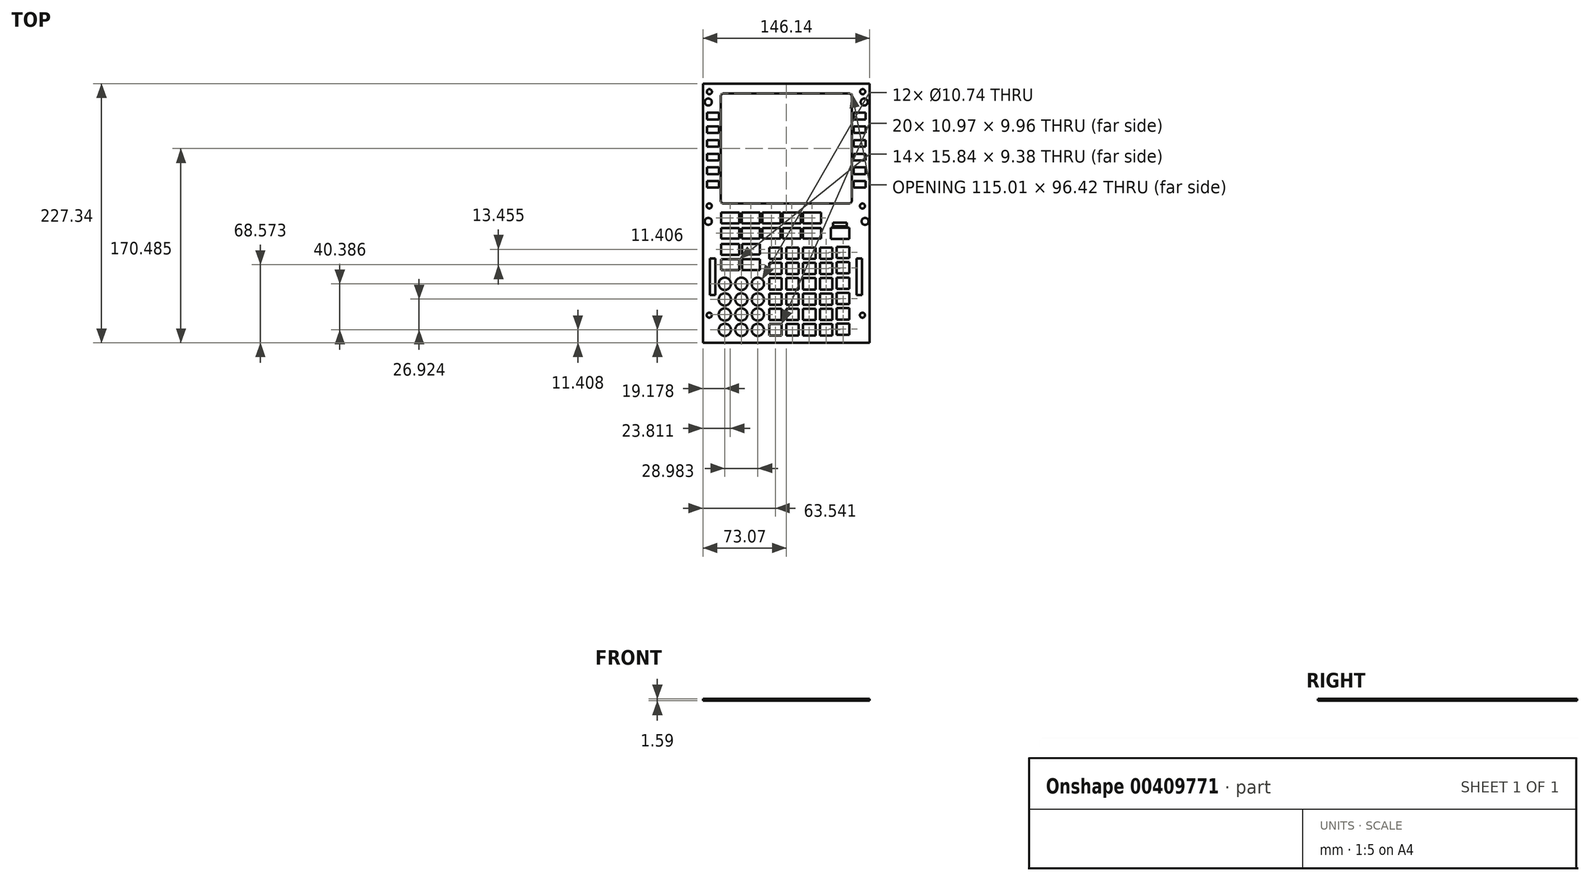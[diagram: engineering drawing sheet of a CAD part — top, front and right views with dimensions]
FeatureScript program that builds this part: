
annotation { "Feature Type Name" : "Feature", "Feature Type Description" : "" }
export const myFeature = defineFeature(function(context is Context, id is Id, definition is map)
    precondition{}
    {
        {
            var Q0;
            Q0=qCreatedBy(makeId("Top.planeOp"),FACE);
            var sketch = newSketch(context, id + "F0", { "sketchPlane" : qUnion([Q0])});
            skLineSegment(sketch, "E0.bottom", {"start": v(73.07, 113.67) * mm, "end": v(-73.07, 113.67) * mm});
            skLineSegment(sketch, "E0.top", {"start": v(73.07, -113.66) * mm, "end": v(-73.07, -113.66) * mm});
            skLineSegment(sketch, "E0.left", {"start": v(73.07, 113.67) * mm, "end": v(73.07, -113.66) * mm});
            skLineSegment(sketch, "E0.right", {"start": v(-73.07, 113.67) * mm, "end": v(-73.07, -113.66) * mm});
            skPoint(sketch, "E0.middle", {"position": v(0, 0) * mm});
            skLineSegment(sketch, "E1", {"start": v(0, 113.67) * mm, "end": v(0, 111.74) * mm});
            skLineSegment(sketch, "E2", {"start": v(-69.57, 102.01) * mm, "end": v(-68.34, 102.01) * mm});
            skLineSegment(sketch, "E3", {"start": v(-68.34, 93.24) * mm, "end": v(-69.57, 93.24) * mm});
            skLineSegment(sketch, "E4", {"start": v(-72.11, 90.7) * mm, "end": v(-72.11, 2.93) * mm});
            skLineSegment(sketch, "E5", {"start": v(-69.57, 0.4) * mm, "end": v(-66.53, 0.4) * mm});
            skLineSegment(sketch, "E6", {"start": v(-63.99, -2.15) * mm, "end": v(-63.99, -30.43) * mm});
            skLineSegment(sketch, "E7", {"start": v(-66.53, -32.97) * mm, "end": v(-68.15, -32.97) * mm});
            skLineSegment(sketch, "E8", {"start": v(-70.69, -35.51) * mm, "end": v(-70.69, -91.63) * mm});
            skLineSegment(sketch, "E9", {"start": v(-68.15, -94.17) * mm, "end": v(-64.1, -94.17) * mm});
            skLineSegment(sketch, "E10", {"start": v(-61.57, -96.71) * mm, "end": v(-61.57, -107.92) * mm});
            skLineSegment(sketch, "E11", {"start": v(-59.03, -110.46) * mm, "end": v(0, -110.46) * mm});
            skLineSegment(sketch, "E12", {"start": v(-72.11, 110.47) * mm, "end": v(-72.11, 108.94) * mm});
            skLineSegment(sketch, "E13", {"start": v(-70.84, 111.74) * mm, "end": v(-69.31, 111.74) * mm});
            skLineSegment(sketch, "E14", {"start": v(-72.11, 108.94) * mm, "end": v(-72.11, 104.55) * mm});
            skLineSegment(sketch, "E15", {"start": v(-69.31, 111.74) * mm, "end": v(0, 111.74) * mm});
            skPoint(sketch, "E16.visualSharp", {"position": v(-72.11, 111.74) * mm});
            skArc(sketch, "E16.filletArc", {"start": v(-70.84, 111.74) * mm, "mid": v(-71.74, 111.36) * mm, "end": v(-72.11, 110.47) * mm});
            skArc(sketch, "E17", {"start": v(-68.34, 93.24) * mm, "mid": v(-63.95, 97.62) * mm, "end": v(-68.34, 102.01) * mm});
            skPoint(sketch, "E18.visualSharp", {"position": v(-61.57, -110.46) * mm});
            skArc(sketch, "E18.filletArc", {"start": v(-61.57, -107.92) * mm, "mid": v(-60.82, -109.71) * mm, "end": v(-59.03, -110.46) * mm});
            skPoint(sketch, "E19.visualSharp", {"position": v(-61.57, -94.17) * mm});
            skArc(sketch, "E19.filletArc", {"start": v(-61.57, -96.71) * mm, "mid": v(-62.31, -94.92) * mm, "end": v(-64.1, -94.17) * mm});
            skPoint(sketch, "E20.visualSharp", {"position": v(-70.69, -94.17) * mm});
            skArc(sketch, "E20.filletArc", {"start": v(-70.69, -91.63) * mm, "mid": v(-69.94, -93.43) * mm, "end": v(-68.15, -94.17) * mm});
            skPoint(sketch, "E21.visualSharp", {"position": v(-70.69, -32.97) * mm});
            skArc(sketch, "E21.filletArc", {"start": v(-68.15, -32.97) * mm, "mid": v(-69.94, -33.72) * mm, "end": v(-70.69, -35.51) * mm});
            skPoint(sketch, "E22.visualSharp", {"position": v(-63.99, -32.97) * mm});
            skArc(sketch, "E22.filletArc", {"start": v(-66.53, -32.97) * mm, "mid": v(-64.73, -32.23) * mm, "end": v(-63.99, -30.43) * mm});
            skPoint(sketch, "E23.visualSharp", {"position": v(-63.99, 0.4) * mm});
            skArc(sketch, "E23.filletArc", {"start": v(-63.99, -2.15) * mm, "mid": v(-64.73, -0.35) * mm, "end": v(-66.53, 0.4) * mm});
            skPoint(sketch, "E24.visualSharp", {"position": v(-72.11, 0.4) * mm});
            skArc(sketch, "E24.filletArc", {"start": v(-72.11, 2.93) * mm, "mid": v(-71.37, 1.14) * mm, "end": v(-69.57, 0.4) * mm});
            skPoint(sketch, "E25.visualSharp", {"position": v(-72.11, 102.01) * mm});
            skArc(sketch, "E25.filletArc", {"start": v(-72.11, 104.55) * mm, "mid": v(-71.37, 102.76) * mm, "end": v(-69.57, 102.01) * mm});
            skPoint(sketch, "E26.visualSharp", {"position": v(-72.11, 93.24) * mm});
            skArc(sketch, "E26.filletArc", {"start": v(-69.57, 93.24) * mm, "mid": v(-71.37, 92.5) * mm, "end": v(-72.11, 90.7) * mm});
            skLineSegment(sketch, "E27.bottom", {"start": v(-59, 22.55) * mm, "end": v(-69.41, 22.55) * mm});
            skLineSegment(sketch, "E27.top", {"start": v(-59, 28.39) * mm, "end": v(-69.41, 28.39) * mm});
            skLineSegment(sketch, "E27.left", {"start": v(-59, 22.55) * mm, "end": v(-59, 28.39) * mm});
            skLineSegment(sketch, "E27.right", {"start": v(-69.41, 22.55) * mm, "end": v(-69.41, 28.39) * mm});
            skPoint(sketch, "E27.middle", {"position": v(-64.2, 25.47) * mm});
            skLineSegment(sketch, "E28.bottom", {"start": v(-59, 34.4) * mm, "end": v(-69.41, 34.4) * mm});
            skLineSegment(sketch, "E28.top", {"start": v(-59, 40.25) * mm, "end": v(-69.41, 40.25) * mm});
            skLineSegment(sketch, "E28.left", {"start": v(-59, 34.4) * mm, "end": v(-59, 40.25) * mm});
            skLineSegment(sketch, "E28.right", {"start": v(-69.41, 34.4) * mm, "end": v(-69.41, 40.25) * mm});
            skPoint(sketch, "E28.middle", {"position": v(-64.2, 37.33) * mm});
            skLineSegment(sketch, "E29.bottom", {"start": v(-59, 46.4) * mm, "end": v(-69.41, 46.4) * mm});
            skLineSegment(sketch, "E29.top", {"start": v(-59, 52.23) * mm, "end": v(-69.41, 52.23) * mm});
            skLineSegment(sketch, "E29.left", {"start": v(-59, 46.4) * mm, "end": v(-59, 52.23) * mm});
            skLineSegment(sketch, "E29.right", {"start": v(-69.41, 46.4) * mm, "end": v(-69.41, 52.23) * mm});
            skPoint(sketch, "E29.middle", {"position": v(-64.2, 49.31) * mm});
            skLineSegment(sketch, "E30.bottom", {"start": v(-59, 58.39) * mm, "end": v(-69.42, 58.39) * mm});
            skLineSegment(sketch, "E30.top", {"start": v(-59, 64.26) * mm, "end": v(-69.42, 64.26) * mm});
            skLineSegment(sketch, "E30.left", {"start": v(-59, 58.39) * mm, "end": v(-59, 64.26) * mm});
            skLineSegment(sketch, "E30.right", {"start": v(-69.42, 58.39) * mm, "end": v(-69.42, 64.26) * mm});
            skPoint(sketch, "E30.middle", {"position": v(-64.2, 61.32) * mm});
            skLineSegment(sketch, "E31.bottom", {"start": v(-59, 70.4) * mm, "end": v(-69.42, 70.4) * mm});
            skLineSegment(sketch, "E31.top", {"start": v(-59, 76.26) * mm, "end": v(-69.42, 76.26) * mm});
            skLineSegment(sketch, "E31.left", {"start": v(-59, 70.4) * mm, "end": v(-59, 76.26) * mm});
            skLineSegment(sketch, "E31.right", {"start": v(-69.42, 70.4) * mm, "end": v(-69.42, 76.26) * mm});
            skPoint(sketch, "E31.middle", {"position": v(-64.2, 73.33) * mm});
            skLineSegment(sketch, "E32.bottom", {"start": v(-59, 82.37) * mm, "end": v(-69.42, 82.37) * mm});
            skLineSegment(sketch, "E32.top", {"start": v(-59, 88.2) * mm, "end": v(-69.42, 88.2) * mm});
            skLineSegment(sketch, "E32.left", {"start": v(-59, 82.37) * mm, "end": v(-59, 88.2) * mm});
            skLineSegment(sketch, "E32.right", {"start": v(-69.42, 82.37) * mm, "end": v(-69.42, 88.2) * mm});
            skPoint(sketch, "E32.middle", {"position": v(-64.2, 85.29) * mm});
            skLineSegment(sketch, "E33", {"start": v(0, 100.27) * mm, "end": v(-50.04, 100.27) * mm});
            skLineSegment(sketch, "E34", {"start": v(-52.58, 97.73) * mm, "end": v(-52.58, 17.05) * mm});
            skLineSegment(sketch, "E35", {"start": v(-50.04, 14.51) * mm, "end": v(0, 14.51) * mm});
            skPoint(sketch, "E36.visualSharp", {"position": v(-52.58, 14.51) * mm});
            skArc(sketch, "E36.filletArc", {"start": v(-52.58, 17.05) * mm, "mid": v(-51.83, 15.26) * mm, "end": v(-50.04, 14.51) * mm});
            skPoint(sketch, "E37.visualSharp", {"position": v(-52.58, 100.27) * mm});
            skArc(sketch, "E37.filletArc", {"start": v(-50.04, 100.27) * mm, "mid": v(-51.83, 99.53) * mm, "end": v(-52.58, 97.73) * mm});
            skLineSegment(sketch, "E38", {"start": v(0, 105.03) * mm, "end": v(-54.96, 105.03) * mm});
            skLineSegment(sketch, "E39", {"start": v(-57.5, 102.49) * mm, "end": v(-57.5, 11.14) * mm});
            skLineSegment(sketch, "E40", {"start": v(-54.96, 8.6) * mm, "end": v(0, 8.6) * mm});
            skLineSegment(sketch, "E41.MirrorCS", {"start": v(59.03, -110.46) * mm, "end": v(0, -110.46) * mm});
            skArc(sketch, "E42.MirrorCS", {"start": v(61.57, -107.92) * mm, "mid": v(60.82, -109.71) * mm, "end": v(59.03, -110.46) * mm});
            skLineSegment(sketch, "E43.MirrorCS", {"start": v(61.57, -96.71) * mm, "end": v(61.57, -107.92) * mm});
            skArc(sketch, "E44.MirrorCS", {"start": v(61.57, -96.71) * mm, "mid": v(62.31, -94.92) * mm, "end": v(64.1, -94.17) * mm});
            skLineSegment(sketch, "E45.MirrorCS", {"start": v(68.15, -94.17) * mm, "end": v(64.1, -94.17) * mm});
            skArc(sketch, "E46.MirrorCS", {"start": v(70.69, -91.63) * mm, "mid": v(69.94, -93.43) * mm, "end": v(68.15, -94.17) * mm});
            skLineSegment(sketch, "E47.MirrorCS", {"start": v(70.69, -35.51) * mm, "end": v(70.69, -91.63) * mm});
            skArc(sketch, "E48.MirrorCS", {"start": v(68.15, -32.97) * mm, "mid": v(69.94, -33.72) * mm, "end": v(70.69, -35.51) * mm});
            skLineSegment(sketch, "E49.MirrorCS", {"start": v(66.53, -32.97) * mm, "end": v(68.15, -32.97) * mm});
            skArc(sketch, "E50.MirrorCS", {"start": v(66.53, -32.97) * mm, "mid": v(64.73, -32.23) * mm, "end": v(63.99, -30.43) * mm});
            skLineSegment(sketch, "E51.MirrorCS", {"start": v(63.99, -2.15) * mm, "end": v(63.99, -30.43) * mm});
            skArc(sketch, "E52.MirrorCS", {"start": v(63.99, -2.15) * mm, "mid": v(64.73, -0.35) * mm, "end": v(66.53, 0.4) * mm});
            skLineSegment(sketch, "E53.MirrorCS", {"start": v(69.57, 0.4) * mm, "end": v(66.53, 0.4) * mm});
            skArc(sketch, "E54.MirrorCS", {"start": v(72.11, 2.93) * mm, "mid": v(71.37, 1.14) * mm, "end": v(69.57, 0.4) * mm});
            skLineSegment(sketch, "E55.MirrorCS", {"start": v(72.11, 90.7) * mm, "end": v(72.11, 2.93) * mm});
            skLineSegment(sketch, "E56.MirrorCS", {"start": v(69.41, 22.55) * mm, "end": v(69.41, 28.39) * mm});
            skLineSegment(sketch, "E57.MirrorCS", {"start": v(59, 22.55) * mm, "end": v(69.41, 22.55) * mm});
            skLineSegment(sketch, "E58.MirrorCS", {"start": v(59, 22.55) * mm, "end": v(59, 28.39) * mm});
            skLineSegment(sketch, "E59.MirrorCS", {"start": v(59, 28.39) * mm, "end": v(69.41, 28.39) * mm});
            skLineSegment(sketch, "E60.MirrorCS", {"start": v(59, 34.4) * mm, "end": v(69.41, 34.4) * mm});
            skLineSegment(sketch, "E61.MirrorCS", {"start": v(59, 34.4) * mm, "end": v(59, 40.25) * mm});
            skLineSegment(sketch, "E62.MirrorCS", {"start": v(59, 40.25) * mm, "end": v(69.41, 40.25) * mm});
            skLineSegment(sketch, "E63.MirrorCS", {"start": v(69.41, 34.4) * mm, "end": v(69.41, 40.25) * mm});
            skLineSegment(sketch, "E64.MirrorCS", {"start": v(59, 46.4) * mm, "end": v(69.41, 46.4) * mm});
            skLineSegment(sketch, "E65.MirrorCS", {"start": v(59, 46.4) * mm, "end": v(59, 52.23) * mm});
            skLineSegment(sketch, "E66.MirrorCS", {"start": v(59, 52.23) * mm, "end": v(69.41, 52.23) * mm});
            skLineSegment(sketch, "E67.MirrorCS", {"start": v(69.41, 46.4) * mm, "end": v(69.41, 52.23) * mm});
            skLineSegment(sketch, "E68.MirrorCS", {"start": v(59, 58.39) * mm, "end": v(69.42, 58.39) * mm});
            skLineSegment(sketch, "E69.MirrorCS", {"start": v(69.42, 58.39) * mm, "end": v(69.42, 64.26) * mm});
            skLineSegment(sketch, "E70.MirrorCS", {"start": v(59, 64.26) * mm, "end": v(69.42, 64.26) * mm});
            skLineSegment(sketch, "E71.MirrorCS", {"start": v(59, 58.39) * mm, "end": v(59, 64.26) * mm});
            skLineSegment(sketch, "E72.MirrorCS", {"start": v(59, 70.4) * mm, "end": v(69.42, 70.4) * mm});
            skLineSegment(sketch, "E73.MirrorCS", {"start": v(69.42, 70.4) * mm, "end": v(69.42, 76.26) * mm});
            skLineSegment(sketch, "E74.MirrorCS", {"start": v(59, 76.26) * mm, "end": v(69.42, 76.26) * mm});
            skLineSegment(sketch, "E75.MirrorCS", {"start": v(59, 70.4) * mm, "end": v(59, 76.26) * mm});
            skLineSegment(sketch, "E76.MirrorCS", {"start": v(59, 82.37) * mm, "end": v(69.42, 82.37) * mm});
            skLineSegment(sketch, "E77.MirrorCS", {"start": v(69.42, 82.37) * mm, "end": v(69.42, 88.2) * mm});
            skLineSegment(sketch, "E78.MirrorCS", {"start": v(59, 88.2) * mm, "end": v(69.42, 88.2) * mm});
            skLineSegment(sketch, "E79.MirrorCS", {"start": v(59, 82.37) * mm, "end": v(59, 88.2) * mm});
            skArc(sketch, "E80.MirrorCS", {"start": v(69.57, 93.24) * mm, "mid": v(71.37, 92.5) * mm, "end": v(72.11, 90.7) * mm});
            skLineSegment(sketch, "E81.MirrorCS", {"start": v(68.34, 93.24) * mm, "end": v(69.57, 93.24) * mm});
            skArc(sketch, "E82.MirrorCS", {"start": v(68.34, 93.24) * mm, "mid": v(63.95, 97.62) * mm, "end": v(68.34, 102.01) * mm});
            skLineSegment(sketch, "E83.MirrorCS", {"start": v(69.57, 102.01) * mm, "end": v(68.34, 102.01) * mm});
            skArc(sketch, "E84.MirrorCS", {"start": v(72.11, 104.55) * mm, "mid": v(71.37, 102.76) * mm, "end": v(69.57, 102.01) * mm});
            skLineSegment(sketch, "E85.MirrorCS", {"start": v(72.11, 108.94) * mm, "end": v(72.11, 104.55) * mm});
            skLineSegment(sketch, "E86.MirrorCS", {"start": v(72.11, 110.47) * mm, "end": v(72.11, 108.94) * mm});
            skArc(sketch, "E87.MirrorCS", {"start": v(70.84, 111.74) * mm, "mid": v(71.74, 111.36) * mm, "end": v(72.11, 110.47) * mm});
            skLineSegment(sketch, "E88.MirrorCS", {"start": v(70.84, 111.74) * mm, "end": v(69.31, 111.74) * mm});
            skLineSegment(sketch, "E89.MirrorCS", {"start": v(69.31, 111.74) * mm, "end": v(0, 111.74) * mm});
            skLineSegment(sketch, "E90.MirrorCS", {"start": v(50.04, 14.51) * mm, "end": v(0, 14.51) * mm});
            skArc(sketch, "E91.MirrorCS", {"start": v(52.58, 17.05) * mm, "mid": v(51.83, 15.26) * mm, "end": v(50.04, 14.51) * mm});
            skLineSegment(sketch, "E92.MirrorCS", {"start": v(52.58, 97.73) * mm, "end": v(52.58, 17.05) * mm});
            skArc(sketch, "E93.MirrorCS", {"start": v(50.04, 100.27) * mm, "mid": v(51.83, 99.53) * mm, "end": v(52.58, 97.73) * mm});
            skLineSegment(sketch, "E94.MirrorCS", {"start": v(0, 100.27) * mm, "end": v(50.04, 100.27) * mm});
            skPoint(sketch, "E95.visualSharp", {"position": v(-57.5, 105.03) * mm});
            skArc(sketch, "E95.filletArc", {"start": v(-54.96, 105.03) * mm, "mid": v(-56.76, 104.28) * mm, "end": v(-57.5, 102.49) * mm});
            skPoint(sketch, "E96.visualSharp", {"position": v(-57.5, 8.6) * mm});
            skArc(sketch, "E96.filletArc", {"start": v(-57.5, 11.14) * mm, "mid": v(-56.76, 9.35) * mm, "end": v(-54.96, 8.6) * mm});
            skLineSegment(sketch, "E97.MirrorCS", {"start": v(54.96, 8.6) * mm, "end": v(0, 8.6) * mm});
            skArc(sketch, "E98.MirrorCS", {"start": v(57.5, 11.14) * mm, "mid": v(56.76, 9.35) * mm, "end": v(54.96, 8.6) * mm});
            skLineSegment(sketch, "E99.MirrorCS", {"start": v(57.5, 102.49) * mm, "end": v(57.5, 11.14) * mm});
            skArc(sketch, "E100.MirrorCS", {"start": v(54.96, 105.03) * mm, "mid": v(56.76, 104.28) * mm, "end": v(57.5, 102.49) * mm});
            skLineSegment(sketch, "E101.MirrorCS", {"start": v(0, 105.03) * mm, "end": v(54.96, 105.03) * mm});
            skCircle(sketch, "E102", {"center": v(-53.9, -61.88) * mm, "radius": 5.37 * mm});
            skCircle(sketch, "E103", {"center": v(-39.39, -61.88) * mm, "radius": 5.37 * mm});
            skCircle(sketch, "E104", {"center": v(-24.9, -61.88) * mm, "radius": 5.37 * mm});
            skCircle(sketch, "E105", {"center": v(-53.9, -75.58) * mm, "radius": 5.37 * mm});
            skCircle(sketch, "E106", {"center": v(-39.39, -75.58) * mm, "radius": 5.37 * mm});
            skCircle(sketch, "E107", {"center": v(-24.9, -75.58) * mm, "radius": 5.37 * mm});
            skCircle(sketch, "E108", {"center": v(-39.39, -88.8) * mm, "radius": 5.37 * mm});
            skCircle(sketch, "E109", {"center": v(-53.9, -88.8) * mm, "radius": 5.37 * mm});
            skCircle(sketch, "E110", {"center": v(-24.9, -88.8) * mm, "radius": 5.37 * mm});
            skCircle(sketch, "E111", {"center": v(-39.39, -102.26) * mm, "radius": 5.37 * mm});
            skCircle(sketch, "E112", {"center": v(-24.9, -102.26) * mm, "radius": 5.37 * mm});
            skCircle(sketch, "E113", {"center": v(-53.9, -102.26) * mm, "radius": 5.37 * mm});
            skLineSegment(sketch, "E114.bottom", {"start": v(-4.04, -29.98) * mm, "end": v(-15.02, -29.98) * mm});
            skLineSegment(sketch, "E114.top", {"start": v(-4.04, -39.93) * mm, "end": v(-15.02, -39.93) * mm});
            skLineSegment(sketch, "E114.left", {"start": v(-4.04, -29.98) * mm, "end": v(-4.04, -39.93) * mm});
            skLineSegment(sketch, "E114.right", {"start": v(-15.02, -29.98) * mm, "end": v(-15.02, -39.93) * mm});
            skPoint(sketch, "E114.middle", {"position": v(-9.53, -34.95) * mm});
            skLineSegment(sketch, "E115.bottom", {"start": v(-4.04, -43.44) * mm, "end": v(-15.02, -43.44) * mm});
            skLineSegment(sketch, "E115.top", {"start": v(-4.04, -53.4) * mm, "end": v(-15.02, -53.4) * mm});
            skLineSegment(sketch, "E115.left", {"start": v(-4.04, -43.44) * mm, "end": v(-4.04, -53.4) * mm});
            skLineSegment(sketch, "E115.right", {"start": v(-15.02, -43.44) * mm, "end": v(-15.02, -53.4) * mm});
            skPoint(sketch, "E115.middle", {"position": v(-9.53, -48.42) * mm});
            skLineSegment(sketch, "E116.bottom", {"start": v(-4.04, -66.85) * mm, "end": v(-15.02, -66.85) * mm});
            skLineSegment(sketch, "E116.top", {"start": v(-4.04, -56.9) * mm, "end": v(-15.02, -56.9) * mm});
            skLineSegment(sketch, "E116.left", {"start": v(-4.04, -66.85) * mm, "end": v(-4.04, -56.9) * mm});
            skLineSegment(sketch, "E116.right", {"start": v(-15.02, -66.85) * mm, "end": v(-15.02, -56.9) * mm});
            skPoint(sketch, "E116.middle", {"position": v(-9.53, -61.88) * mm});
            skLineSegment(sketch, "E117.bottom", {"start": v(-4.04, -80.32) * mm, "end": v(-15.02, -80.32) * mm});
            skLineSegment(sketch, "E117.top", {"start": v(-4.04, -70.36) * mm, "end": v(-15.02, -70.36) * mm});
            skLineSegment(sketch, "E117.left", {"start": v(-4.04, -80.32) * mm, "end": v(-4.04, -70.36) * mm});
            skLineSegment(sketch, "E117.right", {"start": v(-15.02, -80.32) * mm, "end": v(-15.02, -70.36) * mm});
            skPoint(sketch, "E117.middle", {"position": v(-9.53, -75.34) * mm});
            skLineSegment(sketch, "E118.bottom", {"start": v(-4.04, -93.79) * mm, "end": v(-15.02, -93.79) * mm});
            skLineSegment(sketch, "E118.top", {"start": v(-4.04, -83.82) * mm, "end": v(-15.02, -83.82) * mm});
            skLineSegment(sketch, "E118.left", {"start": v(-4.04, -93.79) * mm, "end": v(-4.04, -83.82) * mm});
            skLineSegment(sketch, "E118.right", {"start": v(-15.02, -93.79) * mm, "end": v(-15.02, -83.82) * mm});
            skPoint(sketch, "E118.middle", {"position": v(-9.53, -88.8) * mm});
            skLineSegment(sketch, "E119.bottom", {"start": v(-4.04, -97.28) * mm, "end": v(-15.02, -97.28) * mm});
            skLineSegment(sketch, "E119.top", {"start": v(-4.04, -107.24) * mm, "end": v(-15.02, -107.24) * mm});
            skLineSegment(sketch, "E119.left", {"start": v(-4.04, -97.28) * mm, "end": v(-4.04, -107.24) * mm});
            skLineSegment(sketch, "E119.right", {"start": v(-15.02, -97.28) * mm, "end": v(-15.02, -107.24) * mm});
            skPoint(sketch, "E119.middle", {"position": v(-9.53, -102.26) * mm});
            skLineSegment(sketch, "E120.bottom", {"start": v(10.97, -29.98) * mm, "end": v(0, -29.98) * mm});
            skLineSegment(sketch, "E120.top", {"start": v(10.97, -39.93) * mm, "end": v(0, -39.93) * mm});
            skLineSegment(sketch, "E120.left", {"start": v(10.97, -29.98) * mm, "end": v(10.97, -39.93) * mm});
            skLineSegment(sketch, "E120.right", {"start": v(0, -29.98) * mm, "end": v(0, -39.93) * mm});
            skLineSegment(sketch, "E121.bottom", {"start": v(10.97, -43.44) * mm, "end": v(0, -43.44) * mm});
            skLineSegment(sketch, "E121.top", {"start": v(10.97, -53.4) * mm, "end": v(0, -53.4) * mm});
            skLineSegment(sketch, "E121.left", {"start": v(10.97, -43.44) * mm, "end": v(10.97, -53.4) * mm});
            skLineSegment(sketch, "E121.right", {"start": v(0, -43.44) * mm, "end": v(0, -53.4) * mm});
            skLineSegment(sketch, "E122.bottom", {"start": v(10.97, -66.85) * mm, "end": v(0, -66.85) * mm});
            skLineSegment(sketch, "E122.top", {"start": v(10.97, -56.9) * mm, "end": v(0, -56.9) * mm});
            skLineSegment(sketch, "E122.left", {"start": v(10.97, -66.85) * mm, "end": v(10.97, -56.9) * mm});
            skLineSegment(sketch, "E122.right", {"start": v(0, -66.85) * mm, "end": v(0, -56.9) * mm});
            skLineSegment(sketch, "E123.bottom", {"start": v(10.97, -80.32) * mm, "end": v(0, -80.32) * mm});
            skLineSegment(sketch, "E123.top", {"start": v(10.97, -70.36) * mm, "end": v(0, -70.36) * mm});
            skLineSegment(sketch, "E123.left", {"start": v(10.97, -80.32) * mm, "end": v(10.97, -70.36) * mm});
            skLineSegment(sketch, "E123.right", {"start": v(0, -80.32) * mm, "end": v(0, -70.36) * mm});
            skLineSegment(sketch, "E124.bottom", {"start": v(10.97, -93.79) * mm, "end": v(0, -93.79) * mm});
            skLineSegment(sketch, "E124.top", {"start": v(10.97, -83.82) * mm, "end": v(0, -83.82) * mm});
            skLineSegment(sketch, "E124.left", {"start": v(10.97, -93.79) * mm, "end": v(10.97, -83.82) * mm});
            skLineSegment(sketch, "E124.right", {"start": v(0, -93.79) * mm, "end": v(0, -83.82) * mm});
            skLineSegment(sketch, "E125.bottom", {"start": v(10.97, -97.28) * mm, "end": v(0, -97.28) * mm});
            skLineSegment(sketch, "E125.top", {"start": v(10.97, -107.24) * mm, "end": v(0, -107.24) * mm});
            skLineSegment(sketch, "E125.left", {"start": v(10.97, -97.28) * mm, "end": v(10.97, -107.24) * mm});
            skLineSegment(sketch, "E125.right", {"start": v(0, -97.28) * mm, "end": v(0, -107.24) * mm});
            skLineSegment(sketch, "E126.bottom", {"start": v(25.63, -29.98) * mm, "end": v(14.65, -29.98) * mm});
            skLineSegment(sketch, "E126.top", {"start": v(25.63, -39.93) * mm, "end": v(14.65, -39.93) * mm});
            skLineSegment(sketch, "E126.left", {"start": v(25.63, -29.98) * mm, "end": v(25.63, -39.93) * mm});
            skLineSegment(sketch, "E126.right", {"start": v(14.65, -29.98) * mm, "end": v(14.65, -39.93) * mm});
            skLineSegment(sketch, "E127.bottom", {"start": v(25.63, -43.44) * mm, "end": v(14.65, -43.44) * mm});
            skLineSegment(sketch, "E127.top", {"start": v(25.63, -53.4) * mm, "end": v(14.65, -53.4) * mm});
            skLineSegment(sketch, "E127.left", {"start": v(25.63, -43.44) * mm, "end": v(25.63, -53.4) * mm});
            skLineSegment(sketch, "E127.right", {"start": v(14.65, -43.44) * mm, "end": v(14.65, -53.4) * mm});
            skLineSegment(sketch, "E128.bottom", {"start": v(25.63, -66.85) * mm, "end": v(14.65, -66.85) * mm});
            skLineSegment(sketch, "E128.top", {"start": v(25.63, -56.9) * mm, "end": v(14.65, -56.9) * mm});
            skLineSegment(sketch, "E128.left", {"start": v(25.63, -66.85) * mm, "end": v(25.63, -56.9) * mm});
            skLineSegment(sketch, "E128.right", {"start": v(14.65, -66.85) * mm, "end": v(14.65, -56.9) * mm});
            skLineSegment(sketch, "E129.bottom", {"start": v(25.63, -80.32) * mm, "end": v(14.65, -80.32) * mm});
            skLineSegment(sketch, "E129.top", {"start": v(25.63, -70.36) * mm, "end": v(14.65, -70.36) * mm});
            skLineSegment(sketch, "E129.left", {"start": v(25.63, -80.32) * mm, "end": v(25.63, -70.36) * mm});
            skLineSegment(sketch, "E129.right", {"start": v(14.65, -80.32) * mm, "end": v(14.65, -70.36) * mm});
            skLineSegment(sketch, "E130.bottom", {"start": v(25.63, -93.79) * mm, "end": v(14.65, -93.79) * mm});
            skLineSegment(sketch, "E130.top", {"start": v(25.63, -83.82) * mm, "end": v(14.65, -83.82) * mm});
            skLineSegment(sketch, "E130.left", {"start": v(25.63, -93.79) * mm, "end": v(25.63, -83.82) * mm});
            skLineSegment(sketch, "E130.right", {"start": v(14.65, -93.79) * mm, "end": v(14.65, -83.82) * mm});
            skLineSegment(sketch, "E131.bottom", {"start": v(25.63, -97.28) * mm, "end": v(14.65, -97.28) * mm});
            skLineSegment(sketch, "E131.top", {"start": v(25.63, -107.24) * mm, "end": v(14.65, -107.24) * mm});
            skLineSegment(sketch, "E131.left", {"start": v(25.63, -97.28) * mm, "end": v(25.63, -107.24) * mm});
            skLineSegment(sketch, "E131.right", {"start": v(14.65, -97.28) * mm, "end": v(14.65, -107.24) * mm});
            skLineSegment(sketch, "E132.bottom", {"start": v(40.46, -29.98) * mm, "end": v(29.49, -29.98) * mm});
            skLineSegment(sketch, "E132.top", {"start": v(40.46, -39.93) * mm, "end": v(29.49, -39.93) * mm});
            skLineSegment(sketch, "E132.left", {"start": v(40.46, -29.98) * mm, "end": v(40.46, -39.93) * mm});
            skLineSegment(sketch, "E132.right", {"start": v(29.49, -29.98) * mm, "end": v(29.49, -39.93) * mm});
            skLineSegment(sketch, "E133.bottom", {"start": v(40.46, -43.44) * mm, "end": v(29.49, -43.44) * mm});
            skLineSegment(sketch, "E133.top", {"start": v(40.46, -53.4) * mm, "end": v(29.49, -53.4) * mm});
            skLineSegment(sketch, "E133.left", {"start": v(40.46, -43.44) * mm, "end": v(40.46, -53.4) * mm});
            skLineSegment(sketch, "E133.right", {"start": v(29.49, -43.44) * mm, "end": v(29.49, -53.4) * mm});
            skLineSegment(sketch, "E134.bottom", {"start": v(40.46, -66.85) * mm, "end": v(29.49, -66.85) * mm});
            skLineSegment(sketch, "E134.top", {"start": v(40.46, -56.9) * mm, "end": v(29.49, -56.9) * mm});
            skLineSegment(sketch, "E134.left", {"start": v(40.46, -66.85) * mm, "end": v(40.46, -56.9) * mm});
            skLineSegment(sketch, "E134.right", {"start": v(29.49, -66.85) * mm, "end": v(29.49, -56.9) * mm});
            skLineSegment(sketch, "E135.bottom", {"start": v(40.46, -80.32) * mm, "end": v(29.49, -80.32) * mm});
            skLineSegment(sketch, "E135.top", {"start": v(40.46, -70.36) * mm, "end": v(29.49, -70.36) * mm});
            skLineSegment(sketch, "E135.left", {"start": v(40.46, -80.32) * mm, "end": v(40.46, -70.36) * mm});
            skLineSegment(sketch, "E135.right", {"start": v(29.49, -80.32) * mm, "end": v(29.49, -70.36) * mm});
            skLineSegment(sketch, "E136.bottom", {"start": v(40.46, -93.79) * mm, "end": v(29.49, -93.79) * mm});
            skLineSegment(sketch, "E136.top", {"start": v(40.46, -83.82) * mm, "end": v(29.49, -83.82) * mm});
            skLineSegment(sketch, "E136.left", {"start": v(40.46, -93.79) * mm, "end": v(40.46, -83.82) * mm});
            skLineSegment(sketch, "E136.right", {"start": v(29.49, -93.79) * mm, "end": v(29.49, -83.82) * mm});
            skLineSegment(sketch, "E137.bottom", {"start": v(40.46, -97.28) * mm, "end": v(29.49, -97.28) * mm});
            skLineSegment(sketch, "E137.top", {"start": v(40.46, -107.24) * mm, "end": v(29.49, -107.24) * mm});
            skLineSegment(sketch, "E137.left", {"start": v(40.46, -97.28) * mm, "end": v(40.46, -107.24) * mm});
            skLineSegment(sketch, "E137.right", {"start": v(29.49, -97.28) * mm, "end": v(29.49, -107.24) * mm});
            skLineSegment(sketch, "E138.bottom", {"start": v(55.3, -29.4) * mm, "end": v(44.32, -29.4) * mm});
            skLineSegment(sketch, "E138.top", {"start": v(55.3, -39.36) * mm, "end": v(44.32, -39.36) * mm});
            skLineSegment(sketch, "E138.left", {"start": v(55.3, -29.4) * mm, "end": v(55.3, -39.36) * mm});
            skLineSegment(sketch, "E138.right", {"start": v(44.32, -29.4) * mm, "end": v(44.32, -39.36) * mm});
            skLineSegment(sketch, "E139.bottom", {"start": v(55.3, -42.87) * mm, "end": v(44.32, -42.87) * mm});
            skLineSegment(sketch, "E139.top", {"start": v(55.3, -52.82) * mm, "end": v(44.32, -52.82) * mm});
            skLineSegment(sketch, "E139.left", {"start": v(55.3, -42.87) * mm, "end": v(55.3, -52.82) * mm});
            skLineSegment(sketch, "E139.right", {"start": v(44.32, -42.87) * mm, "end": v(44.32, -52.82) * mm});
            skLineSegment(sketch, "E140.bottom", {"start": v(55.3, -66.28) * mm, "end": v(44.32, -66.28) * mm});
            skLineSegment(sketch, "E140.top", {"start": v(55.3, -56.33) * mm, "end": v(44.32, -56.33) * mm});
            skLineSegment(sketch, "E140.left", {"start": v(55.3, -66.28) * mm, "end": v(55.3, -56.33) * mm});
            skLineSegment(sketch, "E140.right", {"start": v(44.32, -66.28) * mm, "end": v(44.32, -56.33) * mm});
            skLineSegment(sketch, "E141.bottom", {"start": v(55.3, -79.75) * mm, "end": v(44.32, -79.75) * mm});
            skLineSegment(sketch, "E141.top", {"start": v(55.3, -69.79) * mm, "end": v(44.32, -69.79) * mm});
            skLineSegment(sketch, "E141.left", {"start": v(55.3, -79.75) * mm, "end": v(55.3, -69.79) * mm});
            skLineSegment(sketch, "E141.right", {"start": v(44.32, -79.75) * mm, "end": v(44.32, -69.79) * mm});
            skLineSegment(sketch, "E142.bottom", {"start": v(55.3, -93.21) * mm, "end": v(44.32, -93.21) * mm});
            skLineSegment(sketch, "E142.top", {"start": v(55.3, -83.25) * mm, "end": v(44.32, -83.25) * mm});
            skLineSegment(sketch, "E142.left", {"start": v(55.3, -93.21) * mm, "end": v(55.3, -83.25) * mm});
            skLineSegment(sketch, "E142.right", {"start": v(44.32, -93.21) * mm, "end": v(44.32, -83.25) * mm});
            skLineSegment(sketch, "E143.bottom", {"start": v(55.3, -96.71) * mm, "end": v(44.32, -96.71) * mm});
            skLineSegment(sketch, "E143.top", {"start": v(55.3, -106.67) * mm, "end": v(44.32, -106.67) * mm});
            skLineSegment(sketch, "E143.left", {"start": v(55.3, -96.71) * mm, "end": v(55.3, -106.67) * mm});
            skLineSegment(sketch, "E143.right", {"start": v(44.32, -96.71) * mm, "end": v(44.32, -106.67) * mm});
            skLineSegment(sketch, "E144.bottom", {"start": v(61.61, -39.56) * mm, "end": v(66.54, -39.56) * mm});
            skLineSegment(sketch, "E144.top", {"start": v(61.61, -71.64) * mm, "end": v(66.54, -71.64) * mm});
            skLineSegment(sketch, "E144.left", {"start": v(61.61, -39.56) * mm, "end": v(61.61, -71.64) * mm});
            skLineSegment(sketch, "E144.right", {"start": v(66.54, -39.56) * mm, "end": v(66.54, -71.64) * mm});
            skLineSegment(sketch, "E145.bottom", {"start": v(-67, -39.56) * mm, "end": v(-62.07, -39.56) * mm});
            skLineSegment(sketch, "E145.top", {"start": v(-67, -71.64) * mm, "end": v(-62.07, -71.64) * mm});
            skLineSegment(sketch, "E145.left", {"start": v(-67, -39.56) * mm, "end": v(-67, -71.64) * mm});
            skLineSegment(sketch, "E145.right", {"start": v(-62.07, -39.56) * mm, "end": v(-62.07, -71.64) * mm});
            skLineSegment(sketch, "E146", {"start": v(-58.24, 4.59) * mm, "end": v(0, 4.59) * mm});
            skLineSegment(sketch, "E147", {"start": v(57.5, 4.59) * mm, "end": v(0, 4.59) * mm});
            skLineSegment(sketch, "E148", {"start": v(-60.78, -49.72) * mm, "end": v(-60.78, 2.05) * mm});
            skLineSegment(sketch, "E149", {"start": v(-21.53, -52.26) * mm, "end": v(-58.24, -52.26) * mm});
            skLineSegment(sketch, "E150", {"start": v(-19, -28.14) * mm, "end": v(-19, -49.72) * mm});
            skLineSegment(sketch, "E151", {"start": v(-16.45, -25.6) * mm, "end": v(57.5, -25.6) * mm});
            skLineSegment(sketch, "E152", {"start": v(60.04, -23.06) * mm, "end": v(60.04, 2.05) * mm});
            skPoint(sketch, "E153.visualSharp", {"position": v(60.04, 4.59) * mm});
            skArc(sketch, "E153.filletArc", {"start": v(60.04, 2.05) * mm, "mid": v(59.3, 3.85) * mm, "end": v(57.5, 4.59) * mm});
            skPoint(sketch, "E154.visualSharp", {"position": v(60.04, -25.6) * mm});
            skArc(sketch, "E154.filletArc", {"start": v(57.5, -25.6) * mm, "mid": v(59.3, -24.86) * mm, "end": v(60.04, -23.06) * mm});
            skPoint(sketch, "E155.visualSharp", {"position": v(-60.78, 4.59) * mm});
            skArc(sketch, "E155.filletArc", {"start": v(-58.24, 4.59) * mm, "mid": v(-60.03, 3.85) * mm, "end": v(-60.78, 2.05) * mm});
            skPoint(sketch, "E156.visualSharp", {"position": v(-60.78, -52.26) * mm});
            skArc(sketch, "E156.filletArc", {"start": v(-60.78, -49.72) * mm, "mid": v(-60.03, -51.52) * mm, "end": v(-58.24, -52.26) * mm});
            skPoint(sketch, "E157.visualSharp", {"position": v(-19, -52.26) * mm});
            skArc(sketch, "E157.filletArc", {"start": v(-21.53, -52.26) * mm, "mid": v(-19.74, -51.52) * mm, "end": v(-19, -49.72) * mm});
            skPoint(sketch, "E158.visualSharp", {"position": v(-19, -25.6) * mm});
            skArc(sketch, "E158.filletArc", {"start": v(-16.45, -25.6) * mm, "mid": v(-18.25, -26.35) * mm, "end": v(-19, -28.14) * mm});
            skLineSegment(sketch, "E159", {"start": v(-57.18, -8.79) * mm, "end": v(-57.18, 0.6) * mm});
            skLineSegment(sketch, "E160", {"start": v(-41.34, 0.6) * mm, "end": v(-57.18, 0.6) * mm});
            skLineSegment(sketch, "E161", {"start": v(-41.34, -8.79) * mm, "end": v(-57.18, -8.79) * mm});
            skLineSegment(sketch, "E162", {"start": v(-41.34, 0.6) * mm, "end": v(-41.34, -8.79) * mm});
            skLineSegment(sketch, "E163", {"start": v(-57.18, -22.24) * mm, "end": v(-57.18, -12.86) * mm});
            skLineSegment(sketch, "E164", {"start": v(-41.34, -12.86) * mm, "end": v(-57.18, -12.86) * mm});
            skLineSegment(sketch, "E165", {"start": v(-41.34, -22.24) * mm, "end": v(-57.18, -22.24) * mm});
            skLineSegment(sketch, "E166", {"start": v(-41.34, -12.86) * mm, "end": v(-41.34, -22.24) * mm});
            skLineSegment(sketch, "E167", {"start": v(-39.13, -8.79) * mm, "end": v(-39.13, 0.6) * mm});
            skLineSegment(sketch, "E168", {"start": v(-23.3, 0.6) * mm, "end": v(-39.13, 0.6) * mm});
            skLineSegment(sketch, "E169", {"start": v(-23.3, -8.79) * mm, "end": v(-39.13, -8.79) * mm});
            skLineSegment(sketch, "E170", {"start": v(-23.3, 0.6) * mm, "end": v(-23.3, -8.79) * mm});
            skLineSegment(sketch, "E171", {"start": v(-39.13, -22.24) * mm, "end": v(-39.13, -12.86) * mm});
            skLineSegment(sketch, "E172", {"start": v(-23.3, -12.86) * mm, "end": v(-39.13, -12.86) * mm});
            skLineSegment(sketch, "E173", {"start": v(-23.3, -22.24) * mm, "end": v(-39.13, -22.24) * mm});
            skLineSegment(sketch, "E174", {"start": v(-23.3, -12.86) * mm, "end": v(-23.3, -22.24) * mm});
            skLineSegment(sketch, "E175", {"start": v(-21.03, -8.79) * mm, "end": v(-21.03, 0.6) * mm});
            skLineSegment(sketch, "E176", {"start": v(-5.18, 0.6) * mm, "end": v(-21.03, 0.6) * mm});
            skLineSegment(sketch, "E177", {"start": v(-5.18, -8.79) * mm, "end": v(-21.03, -8.79) * mm});
            skLineSegment(sketch, "E178", {"start": v(-5.18, 0.6) * mm, "end": v(-5.18, -8.79) * mm});
            skLineSegment(sketch, "E179", {"start": v(-21.03, -22.24) * mm, "end": v(-21.03, -12.86) * mm});
            skLineSegment(sketch, "E180", {"start": v(-5.18, -12.86) * mm, "end": v(-21.03, -12.86) * mm});
            skLineSegment(sketch, "E181", {"start": v(-5.18, -22.24) * mm, "end": v(-21.03, -22.24) * mm});
            skLineSegment(sketch, "E182", {"start": v(-5.18, -12.86) * mm, "end": v(-5.18, -22.24) * mm});
            skLineSegment(sketch, "E183", {"start": v(-3.15, -8.79) * mm, "end": v(-3.15, 0.6) * mm});
            skLineSegment(sketch, "E184", {"start": v(12.69, 0.6) * mm, "end": v(-3.15, 0.6) * mm});
            skLineSegment(sketch, "E185", {"start": v(12.69, -8.79) * mm, "end": v(-3.15, -8.79) * mm});
            skLineSegment(sketch, "E186", {"start": v(12.69, 0.6) * mm, "end": v(12.69, -8.79) * mm});
            skLineSegment(sketch, "E187", {"start": v(-3.15, -22.24) * mm, "end": v(-3.15, -12.86) * mm});
            skLineSegment(sketch, "E188", {"start": v(12.69, -12.86) * mm, "end": v(-3.15, -12.86) * mm});
            skLineSegment(sketch, "E189", {"start": v(12.69, -22.24) * mm, "end": v(-3.15, -22.24) * mm});
            skLineSegment(sketch, "E190", {"start": v(12.69, -12.86) * mm, "end": v(12.69, -22.24) * mm});
            skLineSegment(sketch, "E191", {"start": v(14.65, -8.79) * mm, "end": v(14.65, 0.6) * mm});
            skLineSegment(sketch, "E192", {"start": v(30.5, 0.6) * mm, "end": v(14.65, 0.6) * mm});
            skLineSegment(sketch, "E193", {"start": v(30.5, -8.79) * mm, "end": v(14.65, -8.79) * mm});
            skLineSegment(sketch, "E194", {"start": v(30.5, 0.6) * mm, "end": v(30.5, -8.79) * mm});
            skLineSegment(sketch, "E195", {"start": v(14.65, -22.24) * mm, "end": v(14.65, -12.86) * mm});
            skLineSegment(sketch, "E196", {"start": v(30.5, -12.86) * mm, "end": v(14.65, -12.86) * mm});
            skLineSegment(sketch, "E197", {"start": v(30.5, -22.24) * mm, "end": v(14.65, -22.24) * mm});
            skLineSegment(sketch, "E198", {"start": v(30.5, -12.86) * mm, "end": v(30.5, -22.24) * mm});
            skLineSegment(sketch, "E199", {"start": v(-57.18, -36.33) * mm, "end": v(-57.18, -26.95) * mm});
            skLineSegment(sketch, "E200", {"start": v(-41.34, -26.95) * mm, "end": v(-57.18, -26.95) * mm});
            skLineSegment(sketch, "E201", {"start": v(-41.34, -36.33) * mm, "end": v(-57.18, -36.33) * mm});
            skLineSegment(sketch, "E202", {"start": v(-41.34, -26.95) * mm, "end": v(-41.34, -36.33) * mm});
            skLineSegment(sketch, "E203", {"start": v(-57.18, -49.79) * mm, "end": v(-57.18, -40.4) * mm});
            skLineSegment(sketch, "E204", {"start": v(-41.34, -40.4) * mm, "end": v(-57.18, -40.4) * mm});
            skLineSegment(sketch, "E205", {"start": v(-41.34, -49.79) * mm, "end": v(-57.18, -49.79) * mm});
            skLineSegment(sketch, "E206", {"start": v(-41.34, -40.4) * mm, "end": v(-41.34, -49.79) * mm});
            skLineSegment(sketch, "E207", {"start": v(-38.83, -36.27) * mm, "end": v(-38.83, -26.89) * mm});
            skLineSegment(sketch, "E208", {"start": v(-23, -26.89) * mm, "end": v(-38.83, -26.89) * mm});
            skLineSegment(sketch, "E209", {"start": v(-23, -36.27) * mm, "end": v(-38.83, -36.27) * mm});
            skLineSegment(sketch, "E210", {"start": v(-23, -26.89) * mm, "end": v(-23, -36.27) * mm});
            skLineSegment(sketch, "E211", {"start": v(-38.83, -49.72) * mm, "end": v(-38.83, -40.34) * mm});
            skLineSegment(sketch, "E212", {"start": v(-23, -40.34) * mm, "end": v(-38.83, -40.34) * mm});
            skLineSegment(sketch, "E213", {"start": v(-23, -49.72) * mm, "end": v(-38.83, -49.72) * mm});
            skLineSegment(sketch, "E214", {"start": v(-23, -40.34) * mm, "end": v(-23, -49.72) * mm});
            skLineSegment(sketch, "E215.bottom", {"start": v(39.23, -12.82) * mm, "end": v(55.26, -12.82) * mm});
            skLineSegment(sketch, "E215.top", {"start": v(39.23, -22.56) * mm, "end": v(55.26, -22.56) * mm});
            skLineSegment(sketch, "E215.left", {"start": v(39.23, -12.82) * mm, "end": v(39.23, -22.56) * mm});
            skLineSegment(sketch, "E215.right", {"start": v(55.26, -12.82) * mm, "end": v(55.26, -22.56) * mm});
            skLineSegment(sketch, "E216.bottom", {"start": v(40.96, -8.15) * mm, "end": v(52.9, -8.15) * mm});
            skLineSegment(sketch, "E216.top", {"start": v(40.96, -11.27) * mm, "end": v(52.9, -11.27) * mm});
            skLineSegment(sketch, "E216.left", {"start": v(40.96, -8.15) * mm, "end": v(40.96, -11.27) * mm});
            skLineSegment(sketch, "E216.right", {"start": v(52.9, -8.15) * mm, "end": v(52.9, -11.27) * mm});
            skCircle(sketch, "E217", {"center": v(-67.53, 6.45) * mm, "radius": 2.22 * mm});
            skCircle(sketch, "E218", {"center": v(-67.41, 106.64) * mm, "radius": 2.22 * mm});
            skCircle(sketch, "E219", {"center": v(67, 106.69) * mm, "radius": 2.22 * mm});
            skCircle(sketch, "E220", {"center": v(66.8, 6.35) * mm, "radius": 2.22 * mm});
            skCircle(sketch, "E221", {"center": v(66.82, -89.44) * mm, "radius": 2.23 * mm});
            skCircle(sketch, "E222", {"center": v(-67.53, -89.38) * mm, "radius": 2.22 * mm});
            skCircle(sketch, "E223", {"center": v(68.34, 97.62) * mm, "radius": 3.07 * mm});
            skCircle(sketch, "E224", {"center": v(-68.34, 97.62) * mm, "radius": 3.07 * mm});
            skCircle(sketch, "E225", {"center": v(69.1, -7.12) * mm, "radius": 3.07 * mm});
            skLineSegment(sketch, "E226", {"start": v(68.34, 97.62) * mm, "end": v(-68.34, 97.62) * mm});
            skCircle(sketch, "E227", {"center": v(-68.34, -7.12) * mm, "radius": 3.08 * mm});
            skSolve(sketch);
        }
        {
            var Q0;
            Q0=makeQuery(id+"F0.imprint","IMPRINT",FACE,{"disambiguationData":[TD([[makeQuery(id+"F0.imprint","IMPRINT",EDGE,{"derivedFrom":sQuery(id+"F0.wireOp",EDGE,"E0.top")}),-1.0]])]});
            var Q1;
            Q1=makeQuery(id+"F0.imprint","IMPRINT",FACE,{"disambiguationData":[TD([[makeQuery(id+"F0.imprint","IMPRINT",EDGE,{"derivedFrom":sQuery(id+"F0.wireOp",EDGE,"E2")}),1.0]])]});
            var Q2;
            Q2=makeQuery(id+"F0.imprint","IMPRINT",FACE,{"disambiguationData":[TD([[makeQuery(id+"F0.imprint","IMPRINT",EDGE,{"derivedFrom":sQuery(id+"F0.wireOp",EDGE,"E146")}),-1.0]])]});
            var Q3;
            {var subQ4=sQuery(id+"F0.wireOp",EDGE,"E3");Q3=makeQuery(id+"F0.imprint","IMPRINT",FACE,{"disambiguationData":[TD([[makeQuery(id+"F0.imprint","IMPRINT",EDGE,{"derivedFrom":subQ4}),1.0]])]});}
            extrude(context, id + "F1", {"entities" : qUnion([Q0, Q1, Q2, Q3]), "depth" : 1.59 * mm});
        }
    });
